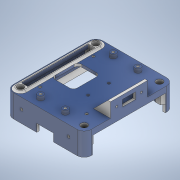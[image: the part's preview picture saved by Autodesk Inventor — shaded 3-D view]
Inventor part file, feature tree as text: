
AUTODESK INVENTOR PART (.ipt)
format: ipt  version: 2022 (Build 260153000, 153)  size: 723,456 bytes
history: native  units: mm
features: sketch x26, extrude x21, mirror x8, fillet x7, hole x5, plane x5
ambient origin geometry x8: Origin, YZ Plane, XZ Plane, XY Plane, X Axis, Y Axis, Z Axis, Center Point
bodies: Solid1 (feature_tree)
feature tree (72):
  extrude  "Extrusion1"  Depth=6.2mm
  extrude  "Extrusion2"  Depth=49.0mm
  extrude  "Extrusion3"  Depth=58.0mm
  extrude  "Extrusion4"  Depth=58.0mm
  extrude  "Extrusion5"  Depth=7.0mm
  hole  "Hole1"  [1 undecoded]
  extrude  "Extrusion6"  Depth=2.0mm TaperAngle=0.0deg
  extrude  "Extrusion8"  Depth=5.0mm
  extrude  "Extrusion12"  Depth=6.5mm
  extrude  "Extrusion13"  Depth=5.0mm
  extrude  "Extrusion14"  Depth=5.0mm TaperAngle=0.0deg
  extrude  "Extrusion15"  Depth=7.0mm
  fillet  "Fillet1"  Radius=17.0mm
  hole  "Hole2"  [1 undecoded]
  extrude  "Extrusion16"  Depth=2.0mm
  extrude  "Extrusion17"  Depth=9.525mm
  hole  "Hole3"  [1 undecoded]
  extrude  "Extrusion18"  Depth=3.0mm TaperAngle=0.0deg
  extrude  "Extrusion19"  Depth=11.0mm
  mirror  "Mirror4"
  extrude  "Extrusion20"  Depth=11.0mm
  hole  "Hole4"  [1 undecoded]
  plane  "Work Plane3"
  mirror  "Mirror5"
  hole  "Hole5"  [1 undecoded]
  extrude  "Extrusion21"  Depth=13.0mm
  plane  "Work Plane4"
  plane  "Work Plane5"
  mirror  "Mirror6"
  mirror  "Mirror7"
  fillet  "Fillet2"  Radius=6.0mm
  fillet  "Fillet3"  Radius=18.0mm
  extrude  "Extrusion22"  Depth=13.0mm
  fillet  "Fillet4"  Radius=13.0mm
  extrude  "Extrusion23"  Depth=2.0mm TaperAngle=0.0deg
  mirror  "Mirror8"
  mirror  "Mirror9"
  fillet  "Fillet5"  Radius=7.15mm
  fillet  "Fillet6"  Radius=7.15mm
  fillet  "Fillet7"  Radius=7.15mm
  extrude  "Extrusion24"  Depth=2.0mm TaperAngle=0.0deg
  extrude  "Extrusion25"  Depth=3.1mm
  mirror  "Mirror10"
  mirror  "Mirror11"
  sketch  "Sketch1"  dims[d0=6.2mm d1=6.2mm]
  sketch  "Sketch2"  dims[d2=6.2mm d3=49.0mm]
  sketch  "Sketch4"  dims[d4=58.0mm d5=6.2mm]
  sketch  "Sketch5"  dims[d6=58.0mm d7=49.0mm]
  sketch  "Sketch6"  dims[d8=10.0mm d9=0.0mm d10=7.0mm]
  sketch  "Sketch7"  dims[d11=7.0mm d12=7.0mm]
  sketch  "Sketch8"  dims[d13=7.0mm d14=2.0mm d15=0.0mm]
  sketch  "Sketch12"  dims[d19=1.0mm d20=5.0mm]
  sketch  "Sketch15"  dims[d21=52.0mm d22=6.5mm]
  sketch  "Sketch16"  dims[d23=2.0mm d24=0.0mm d31=5.0mm]
  sketch  "Sketch17"  dims[d32=5.0mm d33=5.0mm d34=0.0mm]
  sketch  "Sketch18"  dims[d35=20.5mm d36=7.0mm d37=17.0mm]
  sketch  "Sketch19"  dims[d39=5.5mm d40=0.0mm d41=16.0mm]
  sketch  "Sketch20"  dims[d42=2.0mm d43=6.0mm d44=4.0mm d45=2.0mm d46=90.0deg d47=8.0mm d48=20.594885mm d49=2.25mm]
  sketch  "Sketch21"  dims[d50=55.88mm d51=9.525mm]
  sketch  "Sketch22"  dims[d52=4.5mm d53=4.5mm]
  sketch  "Sketch23"  dims[d54=4.6mm d55=3.0mm d56=0.0mm]
  sketch  "Sketch24"  dims[d65=11.0mm d66=11.0mm]
  sketch  "Sketch25"  dims[d67=11.0mm d68=11.0mm]
  sketch  "Sketch26"  dims[d69=17.48mm d70=0.0mm d88=13.0mm]
  sketch  "Sketch27"  dims[d89=1.0mm d90=1.0mm]
  sketch  "Sketch28"  dims[d91=2.0mm d92=0.0mm d93=13.0mm d94=6.0mm d95=18.0mm]
  plane  "Work Plane6"
  plane  "Work Plane7"
  sketch  "Sketch29"  dims[d96=2.0mm d97=0.0mm d98=15.0mm d99=13.0mm]
  sketch  "Sketch30"  dims[d100=20.5mm d101=2.0mm d102=0.0mm d103=7.15mm d104=7.15mm d105=7.15mm]
  sketch  "Sketch32"  dims[d106=7.15mm d107=2.0mm d108=0.0mm]
  sketch  "Sketch34"  dims[d109=3.0mm d110=2.0mm d111=6.0mm d112=5.0mm d113=7.0mm d114=90.0deg d115=8.0mm d116=20.594885mm d117=3.1mm d118=1.0mm d119=2.0mm d120=0.0mm d121=0.0mm d122=14.036mm d123=14.036mm d124=12.1mm d125=12.1mm d126=6.0mm d127=6.0mm d128=6.0mm d129=6.0mm d130=4.0mm d131=0.0mm d132=2.0mm d133=6.0mm d134=5.0mm d135=7.0mm d136=90.0deg d137=8.0mm d138=20.594885mm d139=11.0mm d140=12.25mm d141=5.0mm d142=3.0mm d143=5.0mm d144=1.5mm d145=9.5mm d146=2.0mm d147=0.0mm d148=11.0mm d149=2.0mm d150=0.0mm d151=8.0mm d152=11.9mm d153=11.9mm d154=6.0mm d155=6.0mm d156=4.0mm d157=0.0mm d158=36.2mm d159=2.0mm d160=6.0mm d161=4.0mm d162=2.0mm d163=90.0deg d164=8.0mm d165=20.594885mm d166=2.0mm d167=6.0mm d168=4.0mm d169=2.0mm d170=90.0deg d171=8.0mm d172=20.594885mm d173=0.0mm d174=0.0mm d175=7.0mm d176=2.0mm d177=2.0mm d178=0.0mm d179=3.0mm d180=6.0mm d181=2.0mm d182=0.0mm d183=4.0mm d184=2.0mm d185=2.0mm d186=2.0mm d187=0.0mm d188=8.0mm d189=8.0mm d190=7.3mm d191=2.0mm d192=0.0mm]
note: 5 required parameter values undecoded (feature->parameter linkage not recoverable at this tier; creation-order binding heuristic only, values carry confidence <= 0.55)
